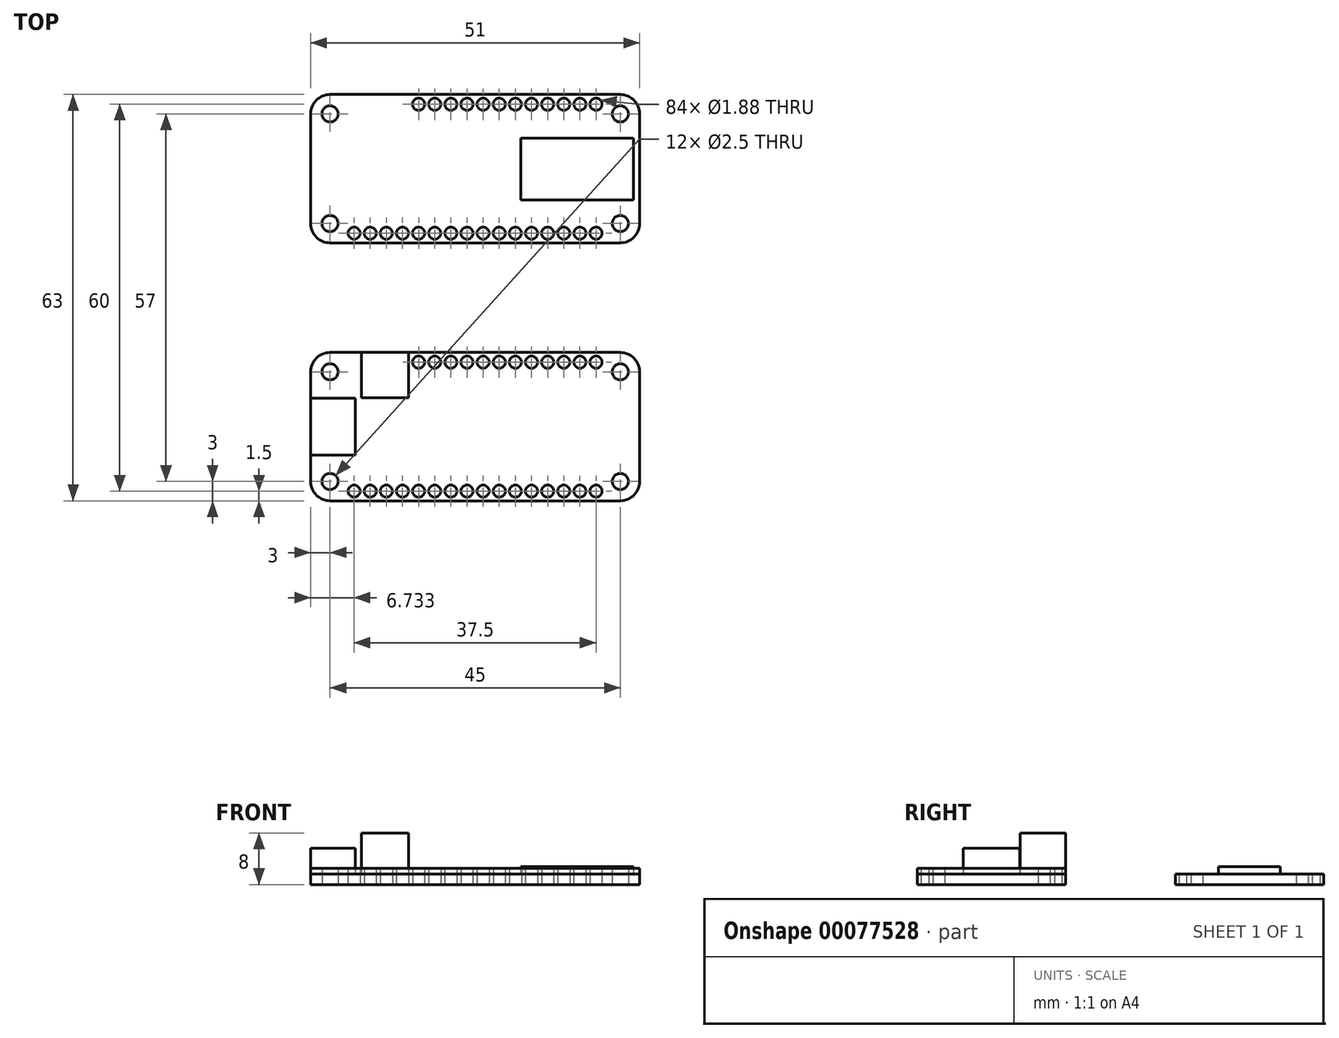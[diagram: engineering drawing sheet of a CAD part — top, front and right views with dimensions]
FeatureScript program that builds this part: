
annotation { "Feature Type Name" : "Feature", "Feature Type Description" : "" }
export const myFeature = defineFeature(function(context is Context, id is Id, definition is map)
    precondition{}
    {
        {
            var Q0;
            Q0=qCreatedBy(makeId("Top.planeOp"),FACE);
            var sketch = newSketch(context, id + "F0", { "sketchPlane" : qUnion([Q0])});
            skLineSegment(sketch, "E0.bottom", {"start": v(-22.5, 11.5) * mm, "end": v(22.5, 11.5) * mm});
            skLineSegment(sketch, "E0.top", {"start": v(-22.5, -11.5) * mm, "end": v(22.5, -11.5) * mm});
            skLineSegment(sketch, "E0.left", {"start": v(-25.5, 8.5) * mm, "end": v(-25.5, -8.5) * mm});
            skLineSegment(sketch, "E0.right", {"start": v(25.5, 8.5) * mm, "end": v(25.5, -8.5) * mm});
            skPoint(sketch, "E0.middle", {"position": v(0, 0) * mm});
            skLineSegment(sketch, "E1.bottom", {"start": v(-22.5, 8.5) * mm, "end": v(22.5, 8.5) * mm, "construction": true});
            skLineSegment(sketch, "E1.top", {"start": v(-22.5, -8.5) * mm, "end": v(22.5, -8.5) * mm, "construction": true});
            skLineSegment(sketch, "E1.left", {"start": v(-22.5, 8.5) * mm, "end": v(-22.5, -8.5) * mm, "construction": true});
            skLineSegment(sketch, "E1.right", {"start": v(22.5, 8.5) * mm, "end": v(22.5, -8.5) * mm, "construction": true});
            skPoint(sketch, "E2.visualSharp", {"position": v(-25.5, 11.5) * mm});
            skArc(sketch, "E2.filletArc", {"start": v(-22.5, 11.5) * mm, "mid": v(-24.62, 10.62) * mm, "end": v(-25.5, 8.5) * mm});
            skPoint(sketch, "E3.visualSharp", {"position": v(25.5, 11.5) * mm});
            skArc(sketch, "E3.filletArc", {"start": v(25.5, 8.5) * mm, "mid": v(24.62, 10.62) * mm, "end": v(22.5, 11.5) * mm});
            skPoint(sketch, "E4.visualSharp", {"position": v(25.5, -11.5) * mm});
            skArc(sketch, "E4.filletArc", {"start": v(22.5, -11.5) * mm, "mid": v(24.62, -10.62) * mm, "end": v(25.5, -8.5) * mm});
            skPoint(sketch, "E5.visualSharp", {"position": v(-25.5, -11.5) * mm});
            skArc(sketch, "E5.filletArc", {"start": v(-25.5, -8.5) * mm, "mid": v(-24.62, -10.62) * mm, "end": v(-22.5, -11.5) * mm});
            skLineSegment(sketch, "E6.bottom", {"start": v(-21.1, 10) * mm, "end": v(21.1, 10) * mm, "construction": true});
            skLineSegment(sketch, "E6.top", {"start": v(-21.1, -10) * mm, "end": v(21.1, -10) * mm, "construction": true});
            skLineSegment(sketch, "E6.left", {"start": v(-21.1, 10) * mm, "end": v(-21.1, -10) * mm, "construction": true});
            skLineSegment(sketch, "E6.right", {"start": v(21.1, 10) * mm, "end": v(21.1, -10) * mm, "construction": true});
            skCircle(sketch, "E7", {"center": v(-22.5, 8.5) * mm, "radius": 1.25 * mm});
            skCircle(sketch, "E8", {"center": v(-22.5, -8.5) * mm, "radius": 1.25 * mm});
            skCircle(sketch, "E9", {"center": v(22.5, -8.5) * mm, "radius": 1.25 * mm});
            skCircle(sketch, "E10", {"center": v(22.5, 8.5) * mm, "radius": 1.25 * mm});
            skCircle(sketch, "E11", {"center": v(-18.77, -10) * mm, "radius": 0.94 * mm});
            skCircle(sketch, "E12.1.0.0", {"center": v(-16.27, -10) * mm, "radius": 0.94 * mm});
            skCircle(sketch, "E12.2.0.0", {"center": v(-13.77, -10) * mm, "radius": 0.94 * mm});
            skCircle(sketch, "E12.3.0.0", {"center": v(-11.27, -10) * mm, "radius": 0.94 * mm});
            skCircle(sketch, "E12.4.0.0", {"center": v(-8.77, -10) * mm, "radius": 0.94 * mm});
            skCircle(sketch, "E12.5.0.0", {"center": v(-6.27, -10) * mm, "radius": 0.94 * mm});
            skCircle(sketch, "E12.6.0.0", {"center": v(-3.77, -10) * mm, "radius": 0.94 * mm});
            skCircle(sketch, "E12.7.0.0", {"center": v(-1.27, -10) * mm, "radius": 0.94 * mm});
            skCircle(sketch, "E12.8.0.0", {"center": v(1.23, -10) * mm, "radius": 0.94 * mm});
            skCircle(sketch, "E12.9.0.0", {"center": v(3.73, -10) * mm, "radius": 0.94 * mm});
            skCircle(sketch, "E12.10.0.0", {"center": v(6.23, -10) * mm, "radius": 0.94 * mm});
            skCircle(sketch, "E12.11.0.0", {"center": v(8.73, -10) * mm, "radius": 0.94 * mm});
            skCircle(sketch, "E12.12.0.0", {"center": v(11.23, -10) * mm, "radius": 0.94 * mm});
            skCircle(sketch, "E12.13.0.0", {"center": v(13.73, -10) * mm, "radius": 0.94 * mm});
            skCircle(sketch, "E12.14.0.0", {"center": v(16.23, -10) * mm, "radius": 0.94 * mm});
            skCircle(sketch, "E12.15.0.0", {"center": v(18.73, -10) * mm, "radius": 0.94 * mm});
            skLineSegment(sketch, "E12.direction1", {"start": v(-18.77, -10) * mm, "end": v(-16.27, -10) * mm, "construction": true});
            skCircle(sketch, "E13", {"center": v(18.73, 10) * mm, "radius": 0.94 * mm});
            skCircle(sketch, "E14.1.0.0", {"center": v(16.23, 10) * mm, "radius": 0.94 * mm});
            skCircle(sketch, "E14.2.0.0", {"center": v(13.73, 10) * mm, "radius": 0.94 * mm});
            skCircle(sketch, "E14.3.0.0", {"center": v(11.23, 10) * mm, "radius": 0.94 * mm});
            skCircle(sketch, "E14.4.0.0", {"center": v(8.73, 10) * mm, "radius": 0.94 * mm});
            skCircle(sketch, "E14.5.0.0", {"center": v(6.23, 10) * mm, "radius": 0.94 * mm});
            skCircle(sketch, "E14.6.0.0", {"center": v(3.73, 10) * mm, "radius": 0.94 * mm});
            skCircle(sketch, "E14.7.0.0", {"center": v(1.23, 10) * mm, "radius": 0.94 * mm});
            skCircle(sketch, "E14.8.0.0", {"center": v(-1.27, 10) * mm, "radius": 0.94 * mm});
            skCircle(sketch, "E14.9.0.0", {"center": v(-3.77, 10) * mm, "radius": 0.94 * mm});
            skCircle(sketch, "E14.10.0.0", {"center": v(-6.27, 10) * mm, "radius": 0.94 * mm});
            skCircle(sketch, "E14.11.0.0", {"center": v(-8.77, 10) * mm, "radius": 0.94 * mm});
            skLineSegment(sketch, "E14.direction1", {"start": v(18.73, 10) * mm, "end": v(16.23, 10) * mm, "construction": true});
            skSolve(sketch);
        }
        {
            var Q0;
            Q0 = qSketchRegion(id + "F0", true);
            extrude(context, id + "F1", {"entities" : qUnion([Q0]), "depth" : 1.6 * mm});
        }
        {
            var Q0;
            Q0=makeQuery(id+"F1.opExtrude","CAP_FACE",FACE,{"disambiguationData":[OSD([sQuery(id+"F0.wireOp",EDGE,"E0.bottom"),sQuery(id+"F0.wireOp",EDGE,"E0.top"),sQuery(id+"F0.wireOp",EDGE,"E0.left"),sQuery(id+"F0.wireOp",EDGE,"E0.right"),sQuery(id+"F0.wireOp",EDGE,"E2.filletArc"),sQuery(id+"F0.wireOp",EDGE,"E3.filletArc"),sQuery(id+"F0.wireOp",EDGE,"E4.filletArc"),sQuery(id+"F0.wireOp",EDGE,"E5.filletArc")])],"isStart":false});
            var sketch = newSketch(context, id + "F2", { "sketchPlane" : qUnion([Q0])});
            skLineSegment(sketch, "E15.bottom", {"start": v(-25.5, 4.38) * mm, "end": v(-18.6, 4.38) * mm});
            skLineSegment(sketch, "E15.top", {"start": v(-25.5, -4.38) * mm, "end": v(-18.6, -4.38) * mm});
            skLineSegment(sketch, "E15.left", {"start": v(-25.5, 4.38) * mm, "end": v(-25.5, -4.38) * mm});
            skLineSegment(sketch, "E15.right", {"start": v(-18.6, 4.38) * mm, "end": v(-18.6, -4.38) * mm});
            skPoint(sketch, "E15.middle", {"position": v(-22.05, 0) * mm});
            skPoint(sketch, "E15.middle.positionSnap0", {"position": v(-25.5, 0) * mm});
            skPoint(sketch, "E15.centerSnap0", {"position": v(-25.5, 0) * mm});
            skLineSegment(sketch, "E16.bottom", {"start": v(-17.62, 11.5) * mm, "end": v(-10.32, 11.5) * mm});
            skLineSegment(sketch, "E16.top", {"start": v(-17.62, 4.46) * mm, "end": v(-10.32, 4.46) * mm});
            skLineSegment(sketch, "E16.left", {"start": v(-17.62, 11.5) * mm, "end": v(-17.62, 4.46) * mm});
            skLineSegment(sketch, "E16.right", {"start": v(-10.32, 11.5) * mm, "end": v(-10.32, 4.46) * mm});
            skSolve(sketch);
        }
        {
            var Q0;
            Q0=makeQuery(id+"F2.imprint","IMPRINT",FACE,{"disambiguationData":[TD([[makeQuery(id+"F2.imprint","IMPRINT",EDGE,{"derivedFrom":sQuery(id+"F2.wireOp",EDGE,"E15.bottom")}),-1.0]])]});
            extrude(context, id + "F3", {"entities" : qUnion([Q0]), "depth" : 4 * mm});
        }
        {
            var Q0;
            Q0=makeQuery(id+"F2.imprint","IMPRINT",FACE,{"disambiguationData":[TD([[makeQuery(id+"F2.imprint","IMPRINT",EDGE,{"derivedFrom":sQuery(id+"F2.wireOp",EDGE,"E16.bottom")}),-1.0]])]});
            extrude(context, id + "F4", {"entities" : qUnion([Q0]), "depth" : (8 - 1.6) * mm});
        }
        {
            var Q0;
            Q0=makeQuery(id+"F1.opExtrude","SWEPT_BODY",BODY,{"disambiguationData":[OSD([sQuery(id+"F0.wireOp",EDGE,"E0.bottom"),sQuery(id+"F0.wireOp",EDGE,"E0.top"),sQuery(id+"F0.wireOp",EDGE,"E0.left"),sQuery(id+"F0.wireOp",EDGE,"E0.right"),sQuery(id+"F0.wireOp",EDGE,"E2.filletArc"),sQuery(id+"F0.wireOp",EDGE,"E3.filletArc"),sQuery(id+"F0.wireOp",EDGE,"E4.filletArc"),sQuery(id+"F0.wireOp",EDGE,"E5.filletArc"),sQuery(id+"F0.wireOp",EDGE,"E7"),sQuery(id+"F0.wireOp",EDGE,"E8"),sQuery(id+"F0.wireOp",EDGE,"E9"),sQuery(id+"F0.wireOp",EDGE,"E10"),sQuery(id+"F0.wireOp",EDGE,"E11"),sQuery(id+"F0.wireOp",EDGE,"E12.1.0.0"),sQuery(id+"F0.wireOp",EDGE,"E12.2.0.0"),sQuery(id+"F0.wireOp",EDGE,"E12.3.0.0"),sQuery(id+"F0.wireOp",EDGE,"E12.4.0.0"),sQuery(id+"F0.wireOp",EDGE,"E12.5.0.0"),sQuery(id+"F0.wireOp",EDGE,"E12.6.0.0"),sQuery(id+"F0.wireOp",EDGE,"E12.7.0.0"),sQuery(id+"F0.wireOp",EDGE,"E12.8.0.0"),sQuery(id+"F0.wireOp",EDGE,"E12.9.0.0"),sQuery(id+"F0.wireOp",EDGE,"E12.10.0.0"),sQuery(id+"F0.wireOp",EDGE,"E12.11.0.0"),sQuery(id+"F0.wireOp",EDGE,"E12.12.0.0"),sQuery(id+"F0.wireOp",EDGE,"E12.13.0.0"),sQuery(id+"F0.wireOp",EDGE,"E12.14.0.0"),sQuery(id+"F0.wireOp",EDGE,"E12.15.0.0"),sQuery(id+"F0.wireOp",EDGE,"E13"),sQuery(id+"F0.wireOp",EDGE,"E14.1.0.0"),sQuery(id+"F0.wireOp",EDGE,"E14.2.0.0"),sQuery(id+"F0.wireOp",EDGE,"E14.3.0.0"),sQuery(id+"F0.wireOp",EDGE,"E14.4.0.0"),sQuery(id+"F0.wireOp",EDGE,"E14.5.0.0"),sQuery(id+"F0.wireOp",EDGE,"E14.6.0.0"),sQuery(id+"F0.wireOp",EDGE,"E14.7.0.0"),sQuery(id+"F0.wireOp",EDGE,"E14.8.0.0"),sQuery(id+"F0.wireOp",EDGE,"E14.9.0.0"),sQuery(id+"F0.wireOp",EDGE,"E14.10.0.0"),sQuery(id+"F0.wireOp",EDGE,"E14.11.0.0")])]});
            transform(context, id + "F5", {"entities" : qUnion([Q0]), "transformType" : TransformType.TRANSLATION_3D, "dx" : 0 * mm, "dy" : 40 * mm, "dz" : 0 * mm, "makeCopy" : true});
        }
        {
            var Q0;
            Q0=makeQuery(id+"F5.opPattern","COPY",FACE,{"derivedFrom":makeQuery(id+"F1.opExtrude","CAP_FACE",FACE,{"disambiguationData":[OSD([sQuery(id+"F0.wireOp",EDGE,"E0.bottom"),sQuery(id+"F0.wireOp",EDGE,"E0.top"),sQuery(id+"F0.wireOp",EDGE,"E0.left"),sQuery(id+"F0.wireOp",EDGE,"E0.right"),sQuery(id+"F0.wireOp",EDGE,"E2.filletArc"),sQuery(id+"F0.wireOp",EDGE,"E3.filletArc"),sQuery(id+"F0.wireOp",EDGE,"E4.filletArc"),sQuery(id+"F0.wireOp",EDGE,"E5.filletArc"),sQuery(id+"F0.wireOp",EDGE,"E7"),sQuery(id+"F0.wireOp",EDGE,"E8"),sQuery(id+"F0.wireOp",EDGE,"E9"),sQuery(id+"F0.wireOp",EDGE,"E10"),sQuery(id+"F0.wireOp",EDGE,"E11"),sQuery(id+"F0.wireOp",EDGE,"E12.1.0.0"),sQuery(id+"F0.wireOp",EDGE,"E12.2.0.0"),sQuery(id+"F0.wireOp",EDGE,"E12.3.0.0"),sQuery(id+"F0.wireOp",EDGE,"E12.4.0.0"),sQuery(id+"F0.wireOp",EDGE,"E12.5.0.0"),sQuery(id+"F0.wireOp",EDGE,"E12.6.0.0"),sQuery(id+"F0.wireOp",EDGE,"E12.7.0.0"),sQuery(id+"F0.wireOp",EDGE,"E12.8.0.0"),sQuery(id+"F0.wireOp",EDGE,"E12.9.0.0"),sQuery(id+"F0.wireOp",EDGE,"E12.10.0.0"),sQuery(id+"F0.wireOp",EDGE,"E12.11.0.0"),sQuery(id+"F0.wireOp",EDGE,"E12.12.0.0"),sQuery(id+"F0.wireOp",EDGE,"E12.13.0.0"),sQuery(id+"F0.wireOp",EDGE,"E12.14.0.0"),sQuery(id+"F0.wireOp",EDGE,"E12.15.0.0"),sQuery(id+"F0.wireOp",EDGE,"E13"),sQuery(id+"F0.wireOp",EDGE,"E14.1.0.0"),sQuery(id+"F0.wireOp",EDGE,"E14.2.0.0"),sQuery(id+"F0.wireOp",EDGE,"E14.3.0.0"),sQuery(id+"F0.wireOp",EDGE,"E14.4.0.0"),sQuery(id+"F0.wireOp",EDGE,"E14.5.0.0"),sQuery(id+"F0.wireOp",EDGE,"E14.6.0.0"),sQuery(id+"F0.wireOp",EDGE,"E14.7.0.0"),sQuery(id+"F0.wireOp",EDGE,"E14.8.0.0"),sQuery(id+"F0.wireOp",EDGE,"E14.9.0.0"),sQuery(id+"F0.wireOp",EDGE,"E14.10.0.0"),sQuery(id+"F0.wireOp",EDGE,"E14.11.0.0")])],"isStart":false}),"instanceName":"1"});
            var sketch = newSketch(context, id + "F6", { "sketchPlane" : qUnion([Q0])});
            skLineSegment(sketch, "E17.bottom", {"start": v(24.53, 35.15) * mm, "end": v(7.1, 35.15) * mm});
            skLineSegment(sketch, "E17.top", {"start": v(24.53, 44.75) * mm, "end": v(7.1, 44.75) * mm});
            skLineSegment(sketch, "E17.left", {"start": v(24.53, 35.15) * mm, "end": v(24.53, 44.75) * mm});
            skLineSegment(sketch, "E17.right", {"start": v(7.1, 35.15) * mm, "end": v(7.1, 44.75) * mm});
            skSolve(sketch);
        }
        {
            var Q0;
            Q0 = qSketchRegion(id + "F6", true);
            extrude(context, id + "F7", {"entities" : qUnion([Q0]), "operationType" : NewBodyOperationType.ADD, "depth" : 1.2 * mm});
        }
        {
            var Q0;
            Q0 = qSketchRegion(id + "F0", true);
            extrude(context, id + "F8", {"entities" : qUnion([Q0]), "depth" : 2.5 * mm});
        }
    });
